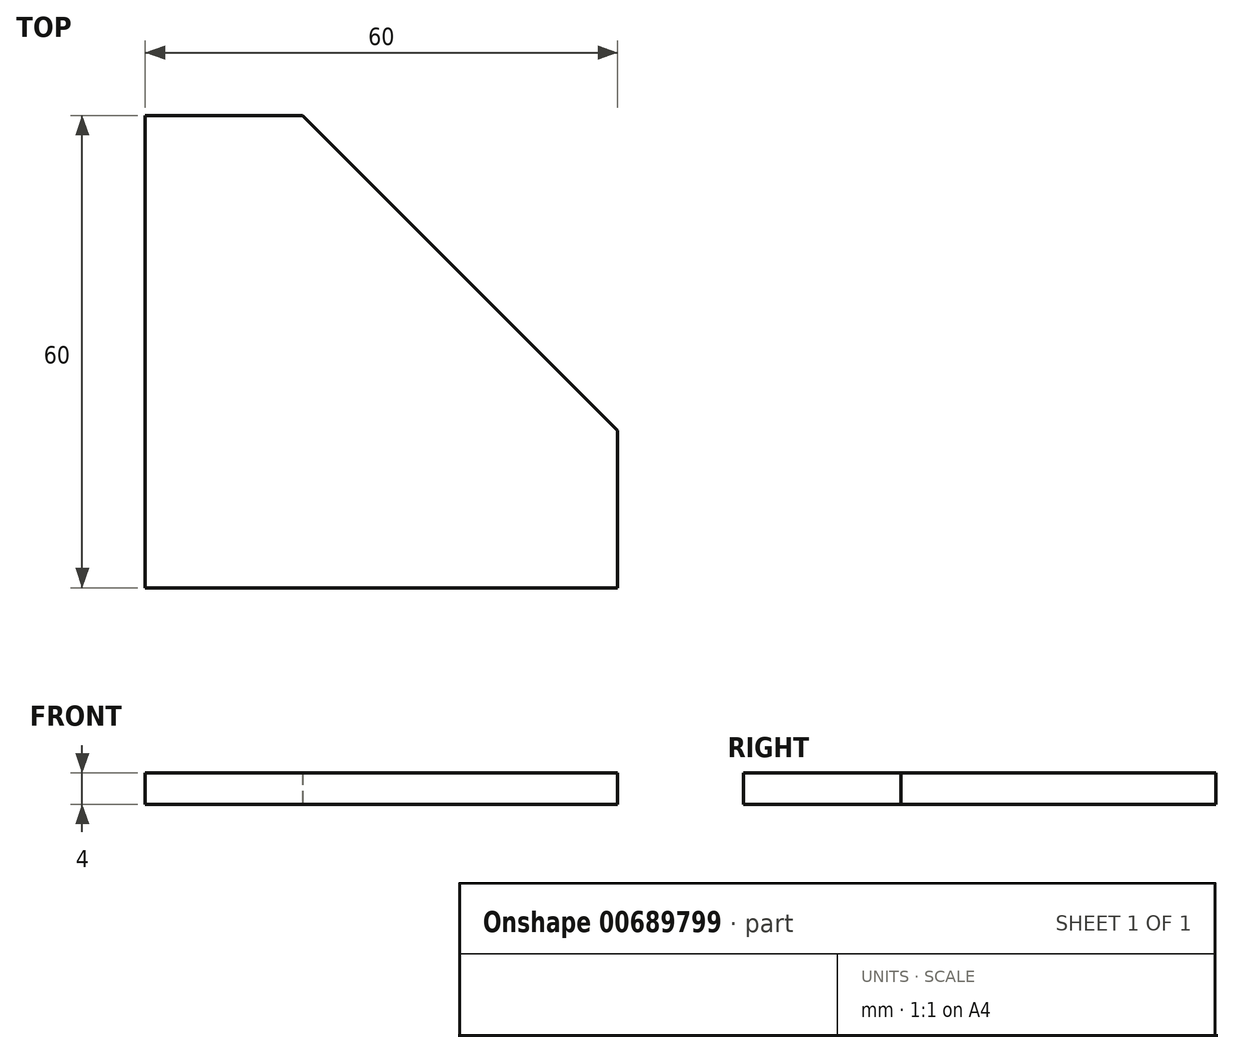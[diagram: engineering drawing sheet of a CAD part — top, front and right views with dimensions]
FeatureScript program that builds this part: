
annotation { "Feature Type Name" : "Feature", "Feature Type Description" : "" }
export const myFeature = defineFeature(function(context is Context, id is Id, definition is map)
    precondition{}
    {
        {
            var Q0;
            Q0=qCreatedBy(makeId("Top.planeOp"),FACE);
            var sketch = newSketch(context, id + "F0", { "sketchPlane" : qUnion([Q0])});
            skLineSegment(sketch, "E0", {"start": v(0, 0) * mm, "end": v(0, 60) * mm});
            skLineSegment(sketch, "E1", {"start": v(0, 60) * mm, "end": v(20, 60) * mm});
            skLineSegment(sketch, "E2", {"start": v(20, 60) * mm, "end": v(60, 20) * mm});
            skLineSegment(sketch, "E3", {"start": v(60, 20) * mm, "end": v(60, 0) * mm});
            skLineSegment(sketch, "E4", {"start": v(60, 0) * mm, "end": v(0, 0) * mm});
            skSolve(sketch);
        }
        {
            var Q0;
            Q0=makeQuery(id+"F0.imprint","IMPRINT",FACE,{"disambiguationData":[TD([[makeQuery(id+"F0.imprint","IMPRINT",EDGE,{"derivedFrom":sQuery(id+"F0.wireOp",EDGE,"E0")}),-1.0]])]});
            extrude(context, id + "F1", {"entities" : qUnion([Q0]), "depth" : 4 * mm, "offsetDistance" : 25 * mm});
        }
    });
